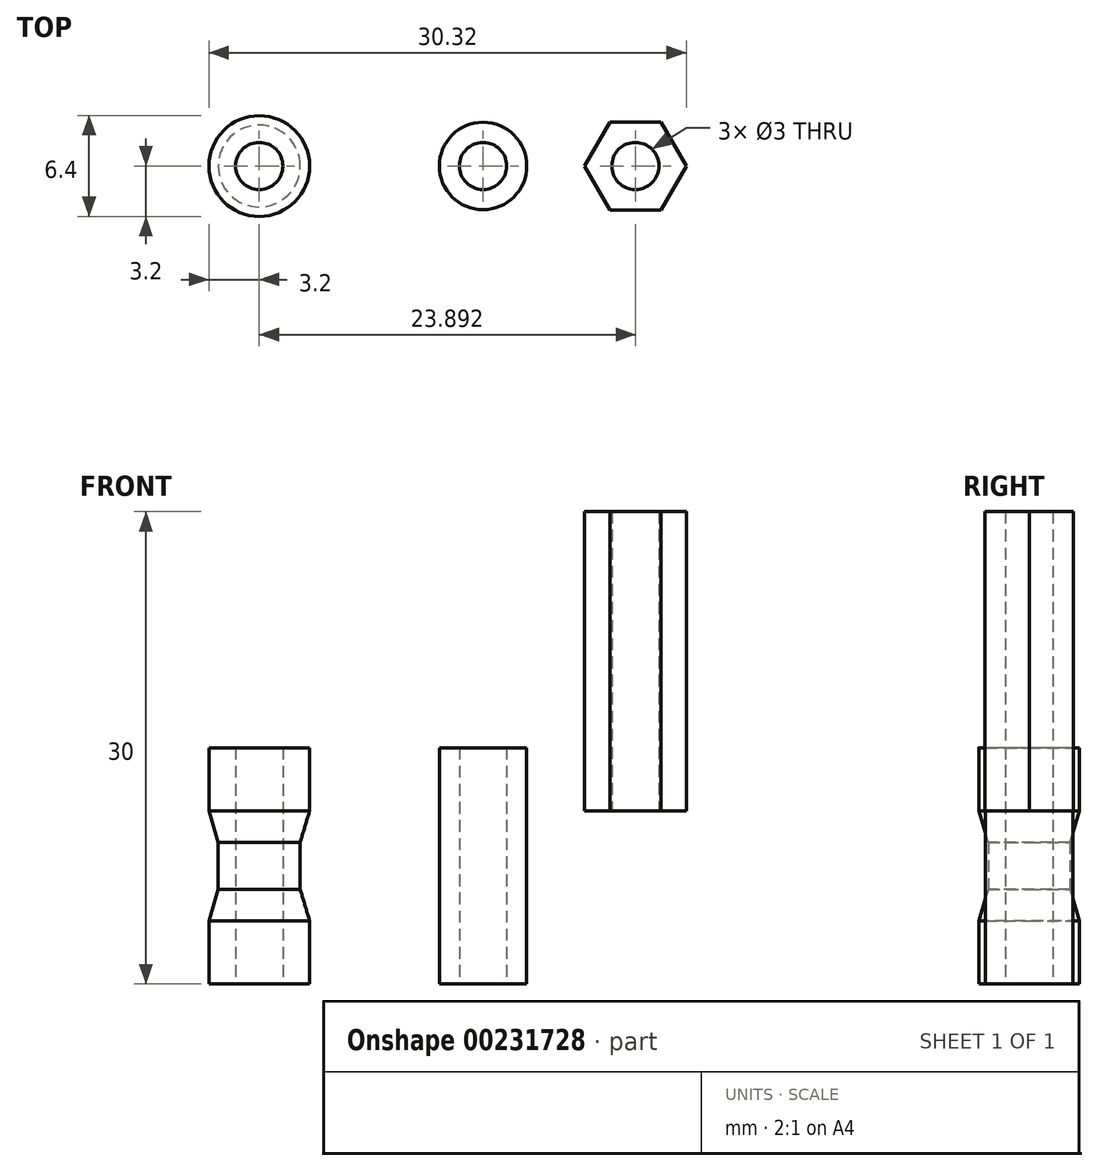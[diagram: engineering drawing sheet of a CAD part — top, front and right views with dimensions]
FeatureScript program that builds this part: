
annotation { "Feature Type Name" : "Feature", "Feature Type Description" : "" }
export const myFeature = defineFeature(function(context is Context, id is Id, definition is map)
    precondition{}
    {
        {
            var Q0;
            Q0=qCreatedBy(makeId("Top.planeOp"),FACE);
            var sketch = newSketch(context, id + "F0", { "sketchPlane" : qUnion([Q0])});
            skCircle(sketch, "E0", {"center": v(0, 0) * mm, "radius": 3.2 * mm});
            skSolve(sketch);
        }
        {
            var Q0;
            Q0 = qSketchRegion(id + "F0", true);
            extrude(context, id + "F1", {"entities" : qUnion([Q0]), "depth" : 4 * mm});
        }
        {
            var Q0;
            Q0=qCreatedBy(makeId("Top.planeOp"),FACE);
            cPlane(context, id + "F2", {"entities" : qUnion([Q0]), "cplaneType" : CPlaneType.OFFSET, "offset" : 6 * mm, "width" : 150 * mm, "height" : 150 * mm});
        }
        {
            var Q0;
            Q0=qCreatedBy(id+"F2.planeOp",FACE);
            var sketch = newSketch(context, id + "F3", { "sketchPlane" : qUnion([Q0])});
            skCircle(sketch, "E1", {"center": v(0, 0) * mm, "radius": 2.6 * mm});
            skSolve(sketch);
        }
        {
            var Q1;
            Q1=makeQuery(id+"F1.opExtrude","CAP_FACE",FACE,{"disambiguationData":[OSD([sQuery(id+"F0.wireOp",EDGE,"E0")])],"isStart":false});
            var Q2;
            Q2=makeQuery(id+"F3.imprint","IMPRINT",FACE,{"disambiguationData":[TD([[makeQuery(id+"F3.imprint","IMPRINT",EDGE,{"derivedFrom":sQuery(id+"F3.wireOp",EDGE,"E1")}),1.0]])]});
            loft(context, id + "F4", {"operationType" : NewBodyOperationType.ADD, "sheetProfilesArray" : [{ "sheetProfileEntities" : qUnion([Q1]) }, { "sheetProfileEntities" : qUnion([Q2]) }]});
        }
        {
            var Q0;
            Q0=qCreatedBy(id+"F2.planeOp",FACE);
            cPlane(context, id + "F5", {"entities" : qUnion([Q0]), "cplaneType" : CPlaneType.OFFSET, "offset" : 3 * mm, "width" : 150 * mm, "height" : 150 * mm});
        }
        {
            var Q0;
            Q0=qCreatedBy(id+"F5.planeOp",FACE);
            var sketch = newSketch(context, id + "F6", { "sketchPlane" : qUnion([Q0])});
            skCircle(sketch, "E2", {"center": v(0, 0) * mm, "radius": 2.6 * mm});
            skSolve(sketch);
        }
        {
            var Q0;
            Q0=qCreatedBy(id+"F5.planeOp",FACE);
            cPlane(context, id + "F7", {"entities" : qUnion([Q0]), "cplaneType" : CPlaneType.OFFSET, "offset" : 2 * mm, "width" : 150 * mm, "height" : 150 * mm});
        }
        {
            var Q0;
            Q0=qCreatedBy(id+"F7.planeOp",FACE);
            var sketch = newSketch(context, id + "F8", { "sketchPlane" : qUnion([Q0])});
            skCircle(sketch, "E3", {"center": v(0, 0) * mm, "radius": 3.2 * mm});
            skSolve(sketch);
        }
        {
            var Q0;
            Q0 = qSketchRegion(id + "F3", true);
            extrude(context, id + "F9", {"entities" : qUnion([Q0]), "operationType" : NewBodyOperationType.ADD, "depth" : 9 * mm});
        }
        {
            var Q1;
            Q1=makeQuery(id+"F6.imprint","IMPRINT",FACE,{"disambiguationData":[TD([[makeQuery(id+"F6.imprint","IMPRINT",EDGE,{"derivedFrom":sQuery(id+"F6.wireOp",EDGE,"E2")}),1.0]])]});
            var Q2;
            Q2=makeQuery(id+"F8.imprint","IMPRINT",FACE,{"disambiguationData":[TD([[makeQuery(id+"F8.imprint","IMPRINT",EDGE,{"derivedFrom":sQuery(id+"F8.wireOp",EDGE,"E3")}),1.0]])]});
            loft(context, id + "F10", {"operationType" : NewBodyOperationType.ADD, "sheetProfilesArray" : [{ "sheetProfileEntities" : qUnion([Q1]) }, { "sheetProfileEntities" : qUnion([Q2]) }]});
        }
        {
            var Q0;
            Q0 = qSketchRegion(id + "F8", true);
            extrude(context, id + "F11", {"entities" : qUnion([Q0]), "operationType" : NewBodyOperationType.ADD, "depth" : 4 * mm});
        }
        {
            var Q0;
            Q0=qCreatedBy(makeId("Top.planeOp"),FACE);
            var sketch = newSketch(context, id + "F12", { "sketchPlane" : qUnion([Q0])});
            skCircle(sketch, "E4", {"center": v(0, 0) * mm, "radius": 1.5 * mm});
            skSolve(sketch);
        }
        {
            var Q0;
            Q0 = qSketchRegion(id + "F12", true);
            extrude(context, id + "F13", {"entities" : qUnion([Q0]), "operationType" : NewBodyOperationType.REMOVE, "depth" : 25 * mm});
        }
        {
            var Q0;
            Q0=qCreatedBy(makeId("Top.planeOp"),FACE);
            var sketch = newSketch(context, id + "F14", { "sketchPlane" : qUnion([Q0])});
            skCircle(sketch, "E5", {"center": v(14.21, 0) * mm, "radius": 2.77 * mm});
            skCircle(sketch, "E6", {"center": v(14.21, 0) * mm, "radius": 1.5 * mm});
            skSolve(sketch);
        }
        {
            var Q0;
            Q0 = qSketchRegion(id + "F14", true);
            extrude(context, id + "F15", {"entities" : qUnion([Q0]), "depth" : 15 * mm, "offsetDistance" : 25 * mm});
        }
        {
            var Q0;
            Q0=qCreatedBy(id+"F7.planeOp",FACE);
            var sketch = newSketch(context, id + "F16", { "sketchPlane" : qUnion([Q0])});
            skCircle(sketch, "E7.cCircle", {"center": v(23.9, 0) * mm, "radius": 2.8 * mm, "construction": true});
            skLineSegment(sketch, "E7.0", {"start": v(22.28, 2.8) * mm, "end": v(25.5, 2.8) * mm});
            skLineSegment(sketch, "E7.1", {"start": v(25.5, 2.8) * mm, "end": v(27.12, 0) * mm});
            skLineSegment(sketch, "E7.2", {"start": v(27.12, 0) * mm, "end": v(25.5, -2.8) * mm});
            skLineSegment(sketch, "E7.3", {"start": v(25.5, -2.8) * mm, "end": v(22.28, -2.8) * mm});
            skLineSegment(sketch, "E7.4", {"start": v(22.28, -2.8) * mm, "end": v(20.66, 0) * mm});
            skLineSegment(sketch, "E7.5", {"start": v(20.66, 0) * mm, "end": v(22.28, 2.8) * mm});
            skPoint(sketch, "E7.0.midPoint", {"position": v(23.9, 2.8) * mm});
            skCircle(sketch, "E8", {"center": v(23.9, 0) * mm, "radius": 1.5 * mm});
            skSolve(sketch);
        }
        {
            var Q0;
            Q0 = qSketchRegion(id + "F16", true);
            extrude(context, id + "F17", {"entities" : qUnion([Q0]), "depth" : 19 * mm, "offsetDistance" : 25 * mm});
        }
    });
